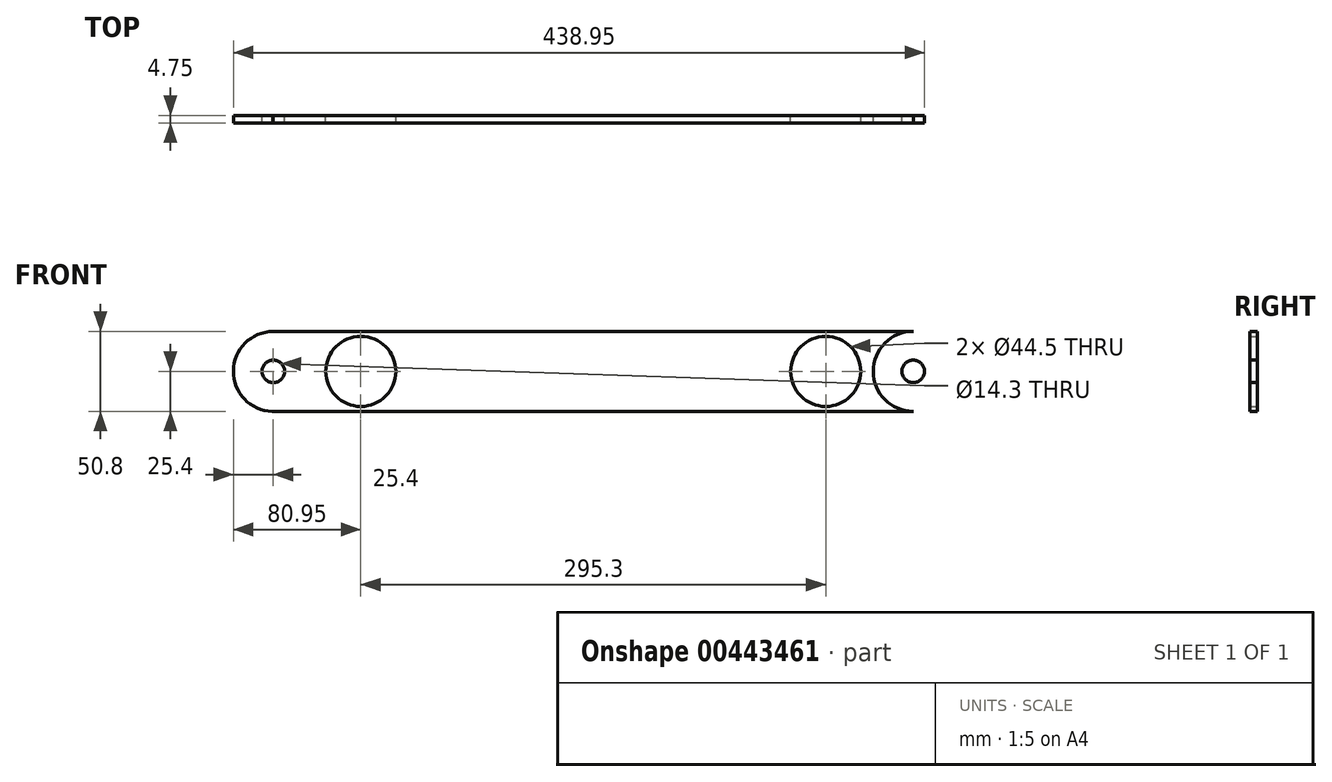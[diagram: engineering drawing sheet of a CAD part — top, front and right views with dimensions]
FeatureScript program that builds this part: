
annotation { "Feature Type Name" : "Feature", "Feature Type Description" : "" }
export const myFeature = defineFeature(function(context is Context, id is Id, definition is map)
    precondition{}
    {
        {
            var Q0;
            Q0=qCreatedBy(makeId("Front.planeOp"),FACE);
            var sketch = newSketch(context, id + "F0", { "sketchPlane" : qUnion([Q0])});
            skCircle(sketch, "E0", {"center": v(-203.2, 0) * mm, "radius": 25.4 * mm});
            skCircle(sketch, "E1", {"center": v(-203.2, 0) * mm, "radius": 7.15 * mm});
            skCircle(sketch, "E2.MirrorC", {"center": v(203.2, 0) * mm, "radius": 25.4 * mm});
            skCircle(sketch, "E3.MirrorC", {"center": v(203.2, 0) * mm, "radius": 7.15 * mm});
            skLineSegment(sketch, "E4", {"start": v(-203.49, 25.4) * mm, "end": v(203.2, 25.4) * mm});
            skLineSegment(sketch, "E5", {"start": v(-203.93, -25.39) * mm, "end": v(203.2, -25.4) * mm});
            skCircle(sketch, "E6", {"center": v(-147.65, 0) * mm, "radius": 22.25 * mm});
            skCircle(sketch, "E7.MirrorC", {"center": v(147.65, 0) * mm, "radius": 22.25 * mm});
            skSolve(sketch);
        }
        {
            var Q0;
            Q0=makeQuery(id+"F0.imprint","IMPRINT",FACE,{"disambiguationData":[TD([[makeQuery(id+"F0.imprint","IMPRINT",EDGE,{"derivedFrom":sQuery(id+"F0.wireOp",EDGE,"E1")}),-1.0]])]});
            var Q1;
            Q1=makeQuery(id+"F0.imprint","IMPRINT",FACE,{"disambiguationData":[TD([[makeQuery(id+"F0.imprint","IMPRINT",EDGE,{"derivedFrom":sQuery(id+"F0.wireOp",EDGE,"E6")}),-1.0]])]});
            var Q2;
            Q2=makeQuery(id+"F0.imprint","IMPRINT",FACE,{"disambiguationData":[TD([[makeQuery(id+"F0.imprint","IMPRINT",EDGE,{"derivedFrom":sQuery(id+"F0.wireOp",EDGE,"E3.MirrorC")}),1.0]])]});
            extrude(context, id + "F1", {"entities" : qUnion([Q0, Q1, Q2]), "depth" : 4.75 * mm});
        }
    });
